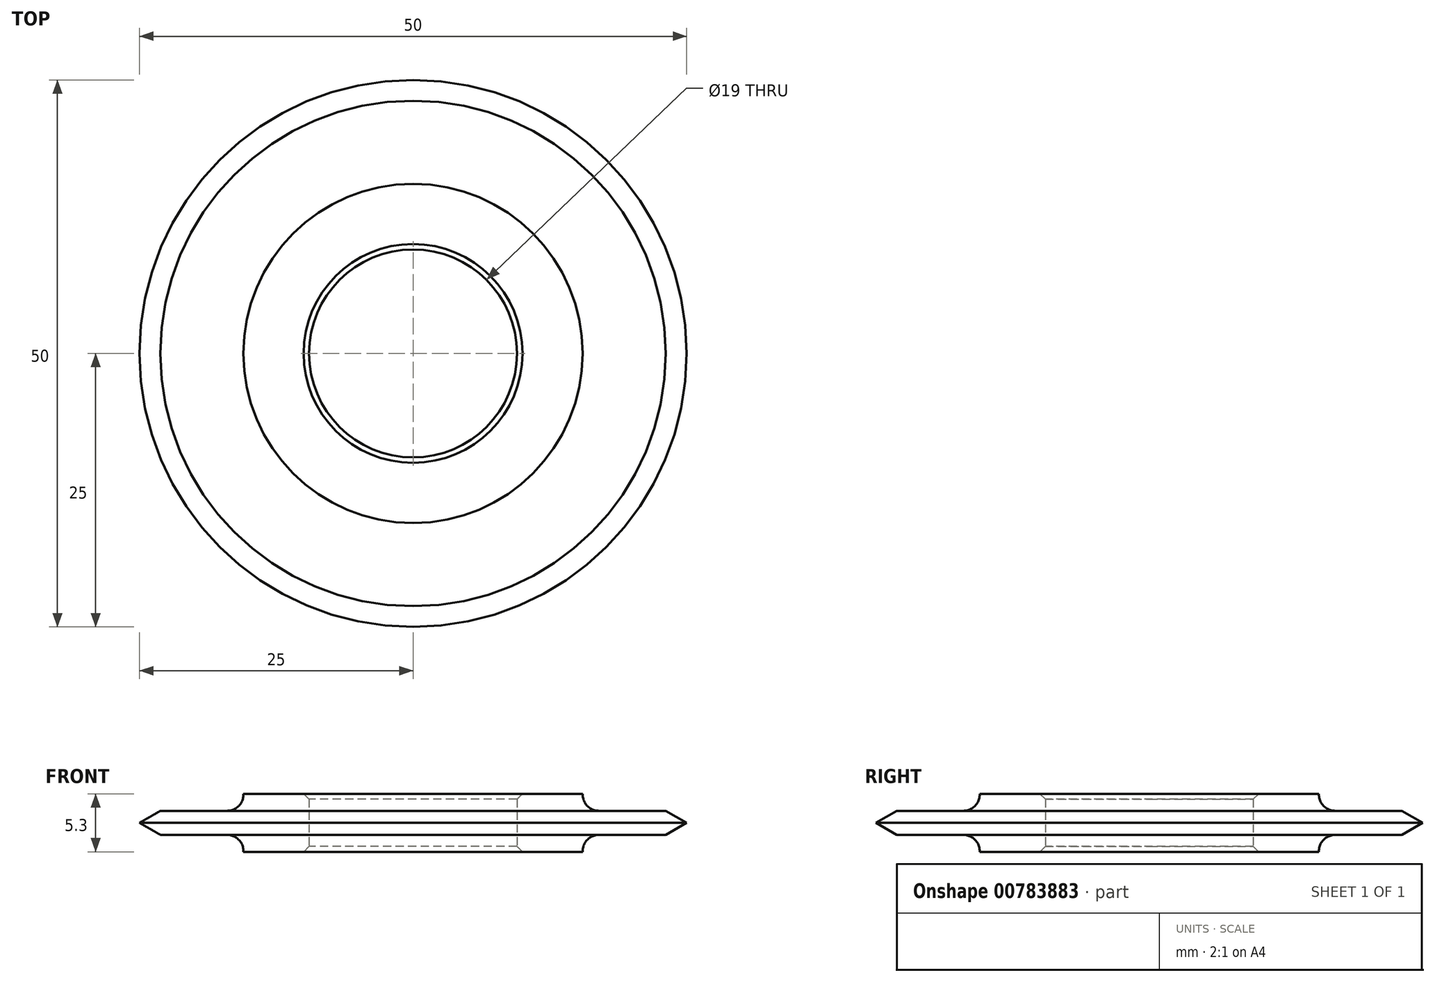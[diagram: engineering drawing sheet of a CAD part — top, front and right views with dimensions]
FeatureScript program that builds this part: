
annotation { "Feature Type Name" : "Feature", "Feature Type Description" : "" }
export const myFeature = defineFeature(function(context is Context, id is Id, definition is map)
    precondition{}
    {
        {
            var Q0;
            Q0=qCreatedBy(makeId("Top.planeOp"),FACE);
            var sketch = newSketch(context, id + "F0", { "sketchPlane" : qUnion([Q0])});
            skCircle(sketch, "E0", {"center": v(0, 0) * mm, "radius": 25 * mm});
            skCircle(sketch, "E1", {"center": v(0, 0) * mm, "radius": 9.5 * mm});
            skSolve(sketch);
        }
        {
            var Q0;
            Q0=makeQuery(id+"F0.imprint","IMPRINT",FACE,{"disambiguationData":[TD([[makeQuery(id+"F0.imprint","IMPRINT",EDGE,{"derivedFrom":sQuery(id+"F0.wireOp",EDGE,"E0")}),1.0]])]});
            extrude(context, id + "F1", {"entities" : qUnion([Q0]), "endBound" : BoundingType.SYMMETRIC, "depth" : 5.3 * mm, "offsetDistance" : 25 * mm});
        }
        {
            var Q0;
            Q0=qCreatedBy(makeId("Front.planeOp"),FACE);
            var sketch = newSketch(context, id + "F2", { "sketchPlane" : qUnion([Q0])});
            skLineSegment(sketch, "E2", {"start": v(9.5, 2.65) * mm, "end": v(9.5, -2.65) * mm});
            skLineSegment(sketch, "E3", {"start": v(25, 2.65) * mm, "end": v(25, -2.65) * mm, "construction": true});
            skLineSegment(sketch, "E4.0.0", {"start": v(-25, 2.65) * mm, "end": v(25, 2.65) * mm, "construction": true});
            skLineSegment(sketch, "E5", {"start": v(15.5, 2.65) * mm, "end": v(15.5, 1.1) * mm});
            skLineSegment(sketch, "E6", {"start": v(15.5, 1.1) * mm, "end": v(23.1, 1.1) * mm});
            skLineSegment(sketch, "E7", {"start": v(23.1, 1.1) * mm, "end": v(25, 0) * mm});
            skLineSegment(sketch, "E8", {"start": v(25, 0) * mm, "end": v(23.1, -1.1) * mm});
            skLineSegment(sketch, "E9", {"start": v(23.1, -1.1) * mm, "end": v(15.5, -1.1) * mm});
            skLineSegment(sketch, "E10", {"start": v(15.5, -1.1) * mm, "end": v(15.5, -2.67) * mm});
            skLineSegment(sketch, "E11", {"start": v(15.5, -2.67) * mm, "end": v(42.87, -11.62) * mm});
            skLineSegment(sketch, "E12", {"start": v(42.87, -11.62) * mm, "end": v(42.87, 12.49) * mm});
            skLineSegment(sketch, "E13", {"start": v(42.87, 12.49) * mm, "end": v(15.5, 2.65) * mm});
            skLineSegment(sketch, "E14", {"start": v(0, 0) * mm, "end": v(0, -6.51) * mm});
            skSolve(sketch);
        }
        {
            var Q0;
            Q0=makeQuery(id+"F2.imprint","IMPRINT",FACE,{"disambiguationData":[TD([[makeQuery(id+"F2.imprint","IMPRINT",EDGE,{"derivedFrom":sQuery(id+"F2.wireOp",EDGE,"E5")}),1.0]])]});
            var Q1;
            Q1=sQuery(id+"F2.wireOp",EDGE,"E14");
            revolve(context, id + "F3", {"operationType" : NewBodyOperationType.REMOVE, "surfaceOperationType" : NewSurfaceOperationType.NEW, "entities" : qUnion([Q0]), "axis" : qUnion([Q1]), "revolveType" : RevolveType.FULL, "oppositeDirection" : true});
        }
        {
            var Q0;
            Q0=makeQuery(id+"F3.boolean.opBoolean","COPY",EDGE,{"derivedFrom":makeQuery(id+"F3.opRevolve","SWEPT_EDGE",EDGE,{"disambiguationData":[OSD([sQuery(id+"F2.wireOp",EDGE,"E5"),sQuery(id+"F2.wireOp",EDGE,"E6")])]})});
            var Q1;
            Q1=makeQuery(id+"F3.boolean.opBoolean","COPY",EDGE,{"derivedFrom":makeQuery(id+"F3.opRevolve","SWEPT_EDGE",EDGE,{"disambiguationData":[OSD([sQuery(id+"F2.wireOp",EDGE,"E9"),sQuery(id+"F2.wireOp",EDGE,"E10")])]})});
            fillet(context, id + "F4", {"entities" : qUnion([Q0, Q1]), "radius" : 1.5 * mm, "tangentPropagation" : true, "allowEdgeOverflow" : false});
        }
        {
            var Q0;
            Q0=makeQuery(id+"F1.opExtrude","CAP_EDGE",EDGE,{"disambiguationData":[OSD([sQuery(id+"F0.wireOp",EDGE,"E1")])],"isStart":false});
            var Q1;
            Q1=makeQuery(id+"F1.opExtrude","CAP_EDGE",EDGE,{"disambiguationData":[OSD([sQuery(id+"F0.wireOp",EDGE,"E1")])],"isStart":true});
            chamfer(context, id + "F5", {"entities" : qUnion([Q0, Q1]), "width" : 0.5 * mm, "tangentPropagation" : true});
        }
    });
